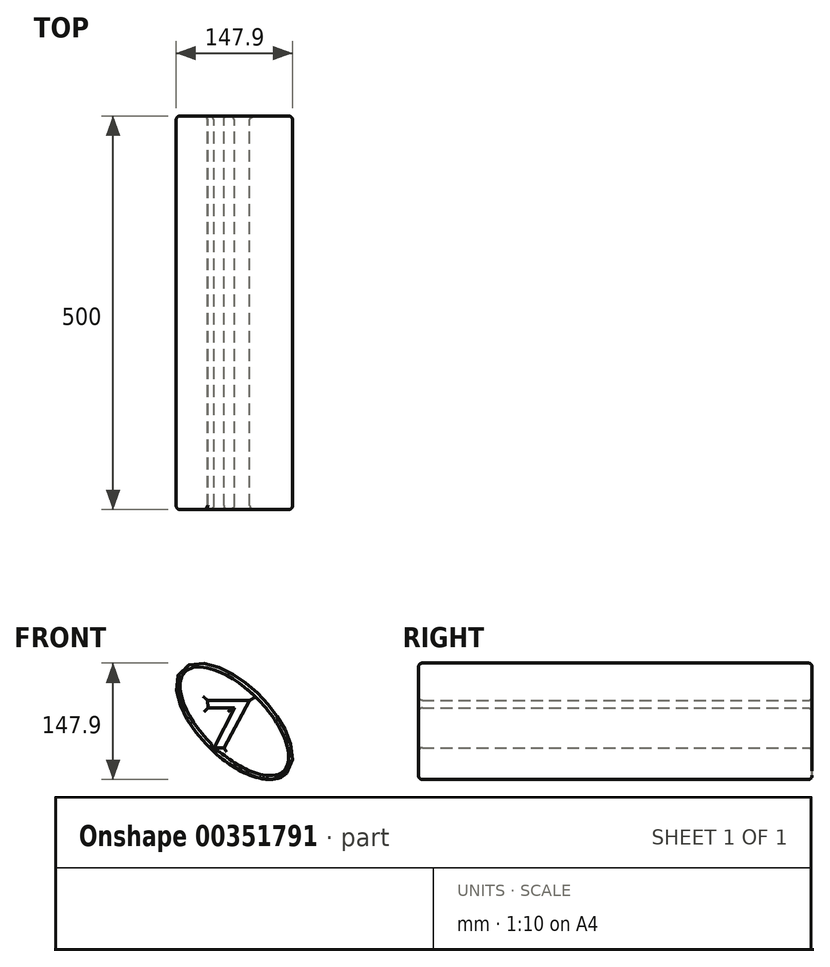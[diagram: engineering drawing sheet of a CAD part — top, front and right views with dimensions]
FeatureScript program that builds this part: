
annotation { "Feature Type Name" : "Feature", "Feature Type Description" : "" }
export const myFeature = defineFeature(function(context is Context, id is Id, definition is map)
    precondition{}
    {
        {
            var Q0;
            Q0=qCreatedBy(makeId("Front.planeOp"),FACE);
            var sketch = newSketch(context, id + "F0", { "sketchPlane" : qUnion([Q0])});
            skEllipse(sketch, "E0", {"center": v(0, 0) * mm, "majorRadius": 93.88 * mm, "minorRadius": 46.08 * mm, "majorAxis": v(0.7, -0.7)});
            skArc(sketch, "E1", {"start": v(0, 58.5) * mm, "mid": v(-41.36, 41.36) * mm, "end": v(-58.5, 0) * mm});
            skArc(sketch, "E2", {"start": v(66.39, -14.84) * mm, "mid": v(48.1, -48.1) * mm, "end": v(14.84, -66.39) * mm});
            skPoint(sketch, "E2.startSnap0", {"position": v(66.39, -66.39) * mm});
            skLineSegment(sketch, "E3", {"start": v(-34.13, 26.6) * mm, "end": v(19.62, 26.6) * mm});
            skLineSegment(sketch, "E4", {"start": v(19.62, 26.6) * mm, "end": v(-13.17, -33.6) * mm});
            skLineSegment(sketch, "E5", {"start": v(-13.17, -33.6) * mm, "end": v(-26.07, -33.6) * mm});
            skLineSegment(sketch, "E6", {"start": v(-26.07, -33.6) * mm, "end": v(0, 16.93) * mm});
            skLineSegment(sketch, "E7", {"start": v(0, 16.93) * mm, "end": v(-33.6, 16.93) * mm});
            skLineSegment(sketch, "E8", {"start": v(-33.6, 16.93) * mm, "end": v(-34.13, 26.6) * mm});
            skSolve(sketch);
        }
        {
            var Q0;
            Q0 = qSketchRegion(id + "F0", true);
            extrude(context, id + "F1", {"entities" : qUnion([Q0]), "depth" : 500 * mm});
        }
        {
            var Q0;
            Q0=makeQuery(id+"F1.opExtrude","CAP_FACE",FACE,{"disambiguationData":[OSD([sQuery(id+"F0.wireOp",EDGE,"E0"),sQuery(id+"F0.wireOp",EDGE,"E3"),sQuery(id+"F0.wireOp",EDGE,"E4"),sQuery(id+"F0.wireOp",EDGE,"E5"),sQuery(id+"F0.wireOp",EDGE,"E6"),sQuery(id+"F0.wireOp",EDGE,"E7"),sQuery(id+"F0.wireOp",EDGE,"E8")])],"isStart":true});
            fillet(context, id + "F2", {"entities" : qUnion([Q0]), "radius" : 5 * mm, "tangentPropagation" : true, "allowEdgeOverflow" : false});
        }
        {
            var Q0;
            Q0=makeQuery(id+"F1.opExtrude","CAP_FACE",FACE,{"disambiguationData":[OSD([sQuery(id+"F0.wireOp",EDGE,"E0"),sQuery(id+"F0.wireOp",EDGE,"E3"),sQuery(id+"F0.wireOp",EDGE,"E4"),sQuery(id+"F0.wireOp",EDGE,"E5"),sQuery(id+"F0.wireOp",EDGE,"E6"),sQuery(id+"F0.wireOp",EDGE,"E7"),sQuery(id+"F0.wireOp",EDGE,"E8")])],"isStart":false});
            fillet(context, id + "F3", {"entities" : qUnion([Q0]), "radius" : 5 * mm, "tangentPropagation" : true, "allowEdgeOverflow" : false});
        }
    });
